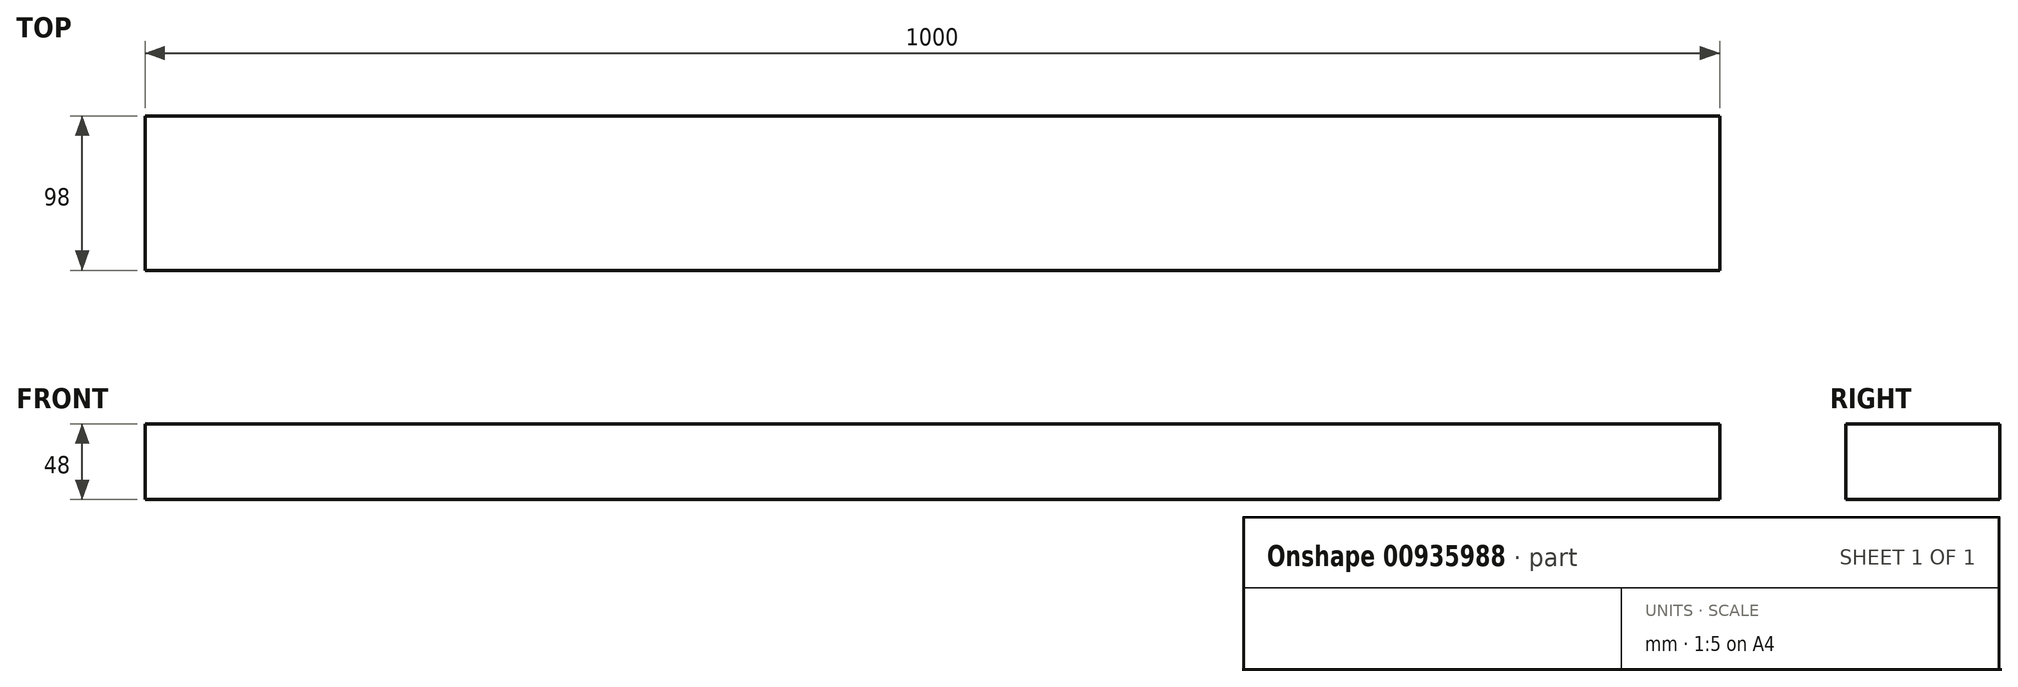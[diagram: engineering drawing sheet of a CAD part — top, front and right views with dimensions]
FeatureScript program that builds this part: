
annotation { "Feature Type Name" : "Feature", "Feature Type Description" : "" }
export const myFeature = defineFeature(function(context is Context, id is Id, definition is map)
    precondition{}
    {
        {
            var Q0;
            Q0=qCreatedBy(makeId("Right.planeOp"),FACE);
            var sketch = newSketch(context, id + "F0", { "sketchPlane" : qUnion([Q0])});
            skLineSegment(sketch, "E0.bottom", {"start": v(49, -24) * mm, "end": v(-49, -24) * mm});
            skLineSegment(sketch, "E0.top", {"start": v(49, 24) * mm, "end": v(-49, 24) * mm});
            skLineSegment(sketch, "E0.left", {"start": v(49, -24) * mm, "end": v(49, 24) * mm});
            skLineSegment(sketch, "E0.right", {"start": v(-49, -24) * mm, "end": v(-49, 24) * mm});
            skPoint(sketch, "E0.middle", {"position": v(0, 0) * mm});
            skSolve(sketch);
        }
        {
            assignVariable(context, id + "F1", {"name" : "Length", "anyValue" : 1000});
        }
        {
            var Q0;
            Q0=qSketchRegion(id+"F0",true);
            extrude(context, id + "F2", {"entities" : qUnion([Q0]), "depth" : (getVariable(context, 'Length')) * mm, "offsetDistance" : 25 * mm});
        }
    });
